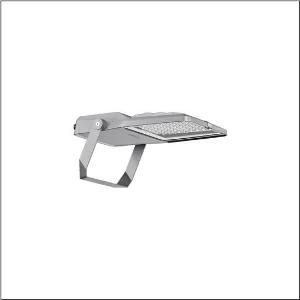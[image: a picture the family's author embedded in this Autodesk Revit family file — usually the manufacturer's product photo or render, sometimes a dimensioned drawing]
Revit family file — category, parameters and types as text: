
# Revit family: floodlight_fl_21_iq_mini___pl52_5xa7772b1d1a_732a
name_source: partatom
category: Lighting Fixtures
units: mm (PartAtom-declared; Revit-internal decimal feet)

## family parameters
Cut with Voids When Loaded = No
Host = Face
Light Source = No
Part Type = Normal
Room Calculation Point = No
Round Connector Dimension = Use Diameter
Shared = No

## types (1)
- --- (1 x LED, 5170 lm, 45.5 W, 2200K)
    Apparent Load = 46 VA
    CIE Flux Codes = 26 60 98 100 100
    Color Rendering = 70
    Color Temperature = 2200K
    Default Elevation = 1800 mm
    Description = Floodlight FL 21 iQ mini, floodlight, primary light control with lens, of PMMA, primary optical cover: protective disc, of toughened safety glass, transparent, light distribution: PL52, light emission: direct distribution, installation type: surface-mounted, lamps: LED, High Power LED, rated values: 5.170lm | 45,5W | 113,6lm/W (begin service life); end service life: 5.170lm | 48W; at 50% lumin. flux: 2.585lm | 21,4W | 120,8lm/W, colour temperature: 2200K, colour rendering: CRI > 70, light colour: 722, light setting 1 begin service life: 100% | 5.170lm | 45,5W | 113,6lm/W | 2.200K, light setting 1 end service life: 48W, further light settings possible, control: Street-Remote, Auto-Match, Temp-Guard, Night-Set, Smart-Wire, Desk-Remote (wireless, voltage-free reading and setting of iQ features in the workshop via application-optimized NFC function/RFID function), optimised constant luminous flux control (CLO 2.0), pre-setting: linear dimming characteristic, with terminal, 6-pole, mains connection: 220..240V, AC, 50/60Hz, luminaire housing, of diecast aluminium, powder-coated, SITECO metallic grey (DB 702S), corrosivity category C5 mid according to DIN EN ISO 12944suitable for swimming poolschlorine-resistant, sealing non-destructively replaceable, mounting bracket, of steel, galvanised, powder-coated, SITECO metallic grey (DB 702S), protection rating (complete): IP66, insulation class (complete): insulation class II (safety insulation), certification: CE, ENEC, VDE, protection symbol: D, impact resistance: IK08, permissible operating ambient temperature: -40..+40°C, permissible operating ambient temperature for outdoor applications: -40..+50°C, standard: DIN EN 12944, LABS conformity tested according to VDMA 24364:2018-05, packaging unit: 1 piece

Light Distribution: PL52
    Height = 70 mm
    Lamp = 1 x LED
    Lamp Light Flux = 5170 lm
    Lamp Power = 45.5 W
    Lamp count = 1
    Length = 485 mm
    Luminous efficacy = 114 lm/W
    Manufacturer = Siteco
    ModVariant = No
    Model = 5XA7772B1D1A
    Mounting Place = Pole
    Mounting Type = Pole annexe
    Number of Poles = 1
    OnlyDefault = Yes
    Power Factor = 1
    Product Name = Floodlight FL 21 iQ mini | PL52
    Product group = floodlight | pylon annexe
    ProductGroupID = 6201
    Protection Class = Protection class II
    Protection Degree = IP 66
    RLX_Detail_Level = 1
    RLX_Emergency_Light_Flux = 0 lm
    RLX_Emergency_Type = 0
    RLX_Emergency_Type_DB = No
    RlxData = <blob elided: 96657 chars, md5=c4670886>
    Socket = socket
    Standby Power = 0 W
    System Light Flux = 5170 lm
    System Power = 46 W
    Type Comments = factory setting: luminous flux: 100 % | dim-lin: 254 | 463 mA
    Type Image = l_1006845.jpg
    URL = http://relux.com
    VarID = @adj_165977
    Voltage = 0 V
    Weight = 0.00 kg
    Width = 337 mm

## geometry (parser evidence)
native form markers: Blend x4, Sweep x11
no freeform markers — native parametric forms only
